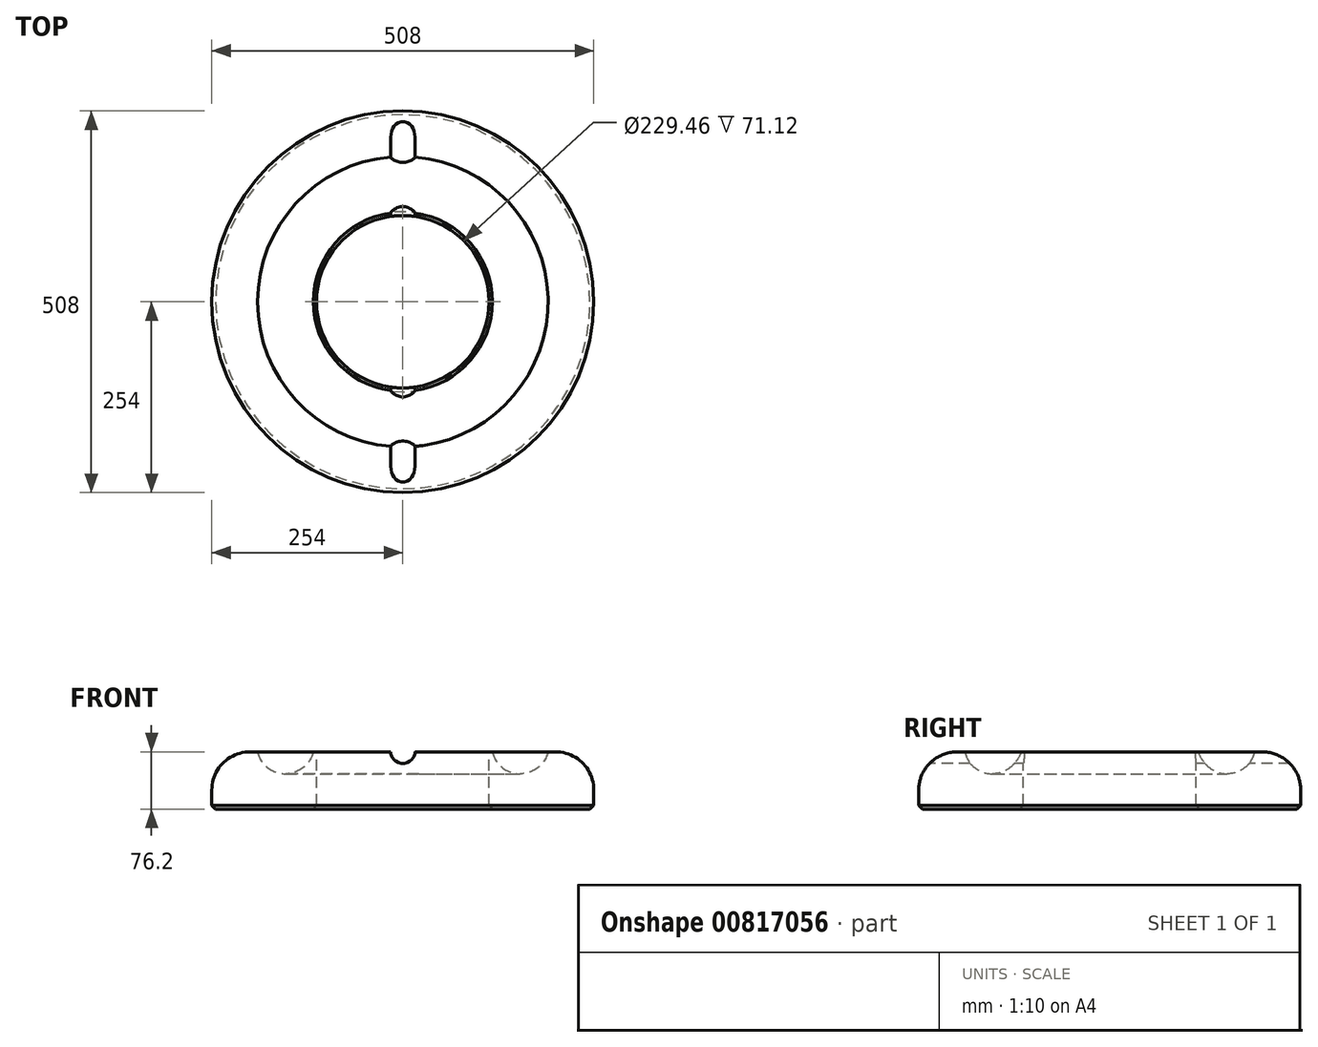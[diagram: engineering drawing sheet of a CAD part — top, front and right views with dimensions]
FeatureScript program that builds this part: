
annotation { "Feature Type Name" : "Feature", "Feature Type Description" : "" }
export const myFeature = defineFeature(function(context is Context, id is Id, definition is map)
    precondition{}
    {
        {
            var Q0;
            Q0=qCreatedBy(makeId("Top.planeOp"),FACE);
            var sketch = newSketch(context, id + "F0", { "sketchPlane" : qUnion([Q0])});
            skCircle(sketch, "E0", {"center": v(0, 0) * mm, "radius": 254 * mm});
            skSolve(sketch);
        }
        {
            var Q0;
            Q0 = qSketchRegion(id + "F0", true);
            extrude(context, id + "F1", {"entities" : qUnion([Q0]), "depth" : 76.2 * mm, "offsetDistance" : 25.4 * mm});
        }
        {
            var Q0;
            Q0=makeQuery(id+"F1.opExtrude","CAP_EDGE",EDGE,{"disambiguationData":[OSD([sQuery(id+"F0.wireOp",EDGE,"E0")])],"isStart":false});
            fillet(context, id + "F2", {"entities" : qUnion([Q0]), "radius" : 50.8 * mm, "tangentPropagation" : true, "allowEdgeOverflow" : false});
        }
        {
            var Q0;
            Q0=makeQuery(id+"F1.opExtrude","CAP_EDGE",EDGE,{"disambiguationData":[OSD([sQuery(id+"F0.wireOp",EDGE,"E0")])],"isStart":true});
            chamfer(context, id + "F3", {"entities" : qUnion([Q0]), "width" : 5.08 * mm, "tangentPropagation" : true});
        }
        {
            var Q0;
            Q0=makeQuery(id+"F1.opExtrude","CAP_FACE",FACE,{"disambiguationData":[OSD([sQuery(id+"F0.wireOp",EDGE,"E0")])],"isStart":false});
            var sketch = newSketch(context, id + "F4", { "sketchPlane" : qUnion([Q0])});
            skCircle(sketch, "E1", {"center": v(0, 0) * mm, "radius": 114.73 * mm});
            skSolve(sketch);
        }
        {
            var Q0;
            Q0 = qSketchRegion(id + "F4", true);
            extrude(context, id + "F5", {"entities" : qUnion([Q0]), "operationType" : NewBodyOperationType.REMOVE, "endBound" : BoundingType.THROUGH_ALL, "oppositeDirection" : true, "depth" : 25.4 * mm, "offsetDistance" : 25.4 * mm});
        }
        {
            var Q0;
            Q0=qCreatedBy(makeId("Front.planeOp"),FACE);
            var sketch = newSketch(context, id + "F6", { "sketchPlane" : qUnion([Q0])});
            skCircle(sketch, "E2", {"center": v(-156.14, 84.99) * mm, "radius": 38.1 * mm});
            skSolve(sketch);
        }
        {
            var Q0;
            Q0=makeQuery(id+"F6.imprint","IMPRINT",FACE,{"disambiguationData":[TD([[makeQuery(id+"F6.imprint","IMPRINT",EDGE,{"derivedFrom":sQuery(id+"F6.wireOp",EDGE,"E2")}),1.0]])]});
            var Q1;
            Q1=makeQuery(id+"F2.opFillet","BLEND_FACE",FACE,{"disambiguationData":[OSD([sQuery(id+"F0.wireOp",EDGE,"E0")])]});
            revolve(context, id + "F7", {"operationType" : NewBodyOperationType.REMOVE, "surfaceOperationType" : NewSurfaceOperationType.NEW, "entities" : qUnion([Q0]), "axis" : qUnion([Q1]), "revolveType" : RevolveType.FULL, "oppositeDirection" : true});
        }
        {
            var Q0;
            Q0=qCreatedBy(makeId("Front.planeOp"),FACE);
            var sketch = newSketch(context, id + "F8", { "sketchPlane" : qUnion([Q0])});
            skCircle(sketch, "E3", {"center": v(0, 77.12) * mm, "radius": 16.4 * mm});
            skSolve(sketch);
        }
        {
            var Q0;
            Q0=makeQuery(id+"F8.imprint","IMPRINT",FACE,{"disambiguationData":[TD([[makeQuery(id+"F8.imprint","IMPRINT",EDGE,{"derivedFrom":sQuery(id+"F8.wireOp",EDGE,"E3")}),1.0]])]});
            extrude(context, id + "F9", {"entities" : qUnion([Q0]), "operationType" : NewBodyOperationType.REMOVE, "endBound" : BoundingType.SYMMETRIC, "oppositeDirection" : true, "depth" : 777.24 * mm, "offsetDistance" : 25.4 * mm});
        }
        {
            var Q0;
            Q0=makeQuery(id+"F5.boolean.opBoolean","INTERSECT",EDGE,{"derivedFrom":[makeQuery(id+"F1.opExtrude","CAP_FACE",FACE,{"disambiguationData":[OSD([sQuery(id+"F0.wireOp",EDGE,"E0")])],"isStart":true}),makeQuery(id+"F5.opExtrude","SWEPT_FACE",FACE,{"disambiguationData":[OSD([sQuery(id+"F4.wireOp",EDGE,"E1")])]})]});
            chamfer(context, id + "F10", {"entities" : qUnion([Q0]), "width" : 5.08 * mm, "tangentPropagation" : true});
        }
    });
